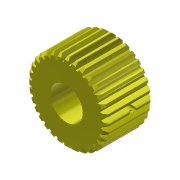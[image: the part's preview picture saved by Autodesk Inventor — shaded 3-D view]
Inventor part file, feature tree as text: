
AUTODESK INVENTOR PART (.ipt)
format: ipt  version: 2019.4 (Build 234330000, 330)  size: 582,144 bytes
history: native  units: mm (DEFAULTED — no unit token found)
features: other x6, sketch x5, extrude x3, plane x3, reference x3, revolve x1
ambient origin geometry x8: Origin, YZ Plane, XZ Plane, XY Plane, X Axis, Y Axis, Z Axis, Center Point
bodies: Solid1 (feature_tree)
feature tree (21):
  extrude  "Extrusion1"  Depth=20.0mm TaperAngle=0.0deg
  plane  "Work Plane2"
  plane  "Work Plane8"
  plane  "Work Plane9"
  other  "Spur Gear"
  extrude  "Extrusion2"  Depth=10.0mm TaperAngle=0.0deg
  extrude  "Extrusion3"  Depth=0.981748mm TaperAngle=0.0deg
  revolve  "Revolution1"  [1 undecoded]
  sketch  "Sketch1"  dims[d0=34.0mm d1=20.0mm d2=0.0mm]
  sketch  "Sketch2"  dims[d3=32.0mm d4=10.0mm d5=0.0mm]
  other  "Srf1"
  sketch  "Sketch3"  dims[d16=29.5mm d17=0.0mm d34=0.981748mm]
  reference  "Reference1"
  sketch  "Sketch4"  dims[d39=0.0mm d41=0.0mm]
  reference  "Reference2"
  sketch  "Sketch5"  dims[d43=29.5mm d46=29.5mm d47=0.0mm d48=0.0mm d49=0.25mm d50=10.0mm d51=-0.087266mm d52=2.9mm d53=2.9mm d54=0.0mm d55=135.0deg d56=90.0deg]
  reference  "Reference3"
  other  "Pitch Diameter"
  other  "cellSTORM_UC2_motorized_micrometer.iam"
  other  "00_micrometer_xy-stage:1"
  other  "Spur Gear2:2"
note: 1 required parameter value undecoded (feature->parameter linkage not recoverable at this tier; creation-order binding heuristic only, values carry confidence <= 0.55)
